# Revit family: СКМ-2К DN15-40 (резьба)
name_source: partatom
category: Арматура трубопроводов
revit_build: Autodesk Revit 2015 (Build: 20140322_1515(x64)
units: mm (PartAtom-declared; Revit-internal decimal feet)

## types (8) — shared parameters
URL = http://vogez.by
Видимость клапана = Да
Длина привода = 4 1/4"
Изготовитель = ООО "ВОГЕЗЭНЕРГО"
Класс точности = 2
Максимальная температура среды = 150 °C
Материал и цвет остальных элементов = Сталь, неокрашенная
Материал и цвет привода ППР = Пластик, серый
Материал и цвет теплосчётчика = Латунь
Наименование = Теплосчётчик
Номинальное давление PN = 1.6 МПа
Скругления привода = 3/4"
Степень защиты = IP55
Ширина привода = 3 1/4"

## per-type parameters (varying)
| type | Высота основания привода | Высота с приводом | Диаметр корпуса | Диаметр условный | Диаметр штока | Максимальный расход | Масса | Минимальный расход | Монтажная длина | Номинальный расход | Обозначение | Тип, марка |
| Теплосчётчик СКМ-2К DN15, q=1,5 м3/ч, L=110 мм | 1 3/4" | 3 1/4" | 3/4" | 1/2" | 3/4" | 3.0 м³/ч | 1.00 kg | 0.0 м³/ч | 4 1/4" | 1.5 м³/ч | СКМ-2К-15-16-55-200 | СКМ-2К-15-16-55-200 |
| Теплосчётчик СКМ-2К DN15, q=1,5 м3/ч, L=165 мм | 1 3/4" | 3 1/4" | 3/4" | 1/2" | 3/4" | 3.0 м³/ч | 1.00 kg | 0.0 м³/ч | 6 1/2" | 1.5 м³/ч | СКМ-2К-15-16-55-200 | СКМ-2К-15-16-55-200 |
| Теплосчётчик СКМ-2К DN20, q=1,5 м3/ч, L=190 мм | 2" | 3 1/2" | 1" | 3/4" | 1" | 5.0 м³/ч | 2.00 kg | 0.1 м³/ч | 7 1/2" | 1.5 м³/ч | СКМ-2К-20-16-55-200 | СКМ-2К-20-16-55-200 |
| Теплосчётчик СКМ-2К DN20, q=2,5 м3/ч, L=190 мм | 2" | 3 1/2" | 1" | 3/4" | 1" | 5.0 м³/ч | 2.00 kg | 0.1 м³/ч | 7 1/2" | 2.5 м³/ч | СКМ-2К-20-16-55-200 | СКМ-2К-20-16-55-200 |
| Теплосчётчик СКМ-2К DN25, q=3,5 м3/ч, L=260 мм | 2 1/4" | 3 3/4" | 1 1/4" | 1" | 1 1/4" | 7.0 м³/ч | 3.00 kg | 0.1 м³/ч | 10 1/4" | 3.5 м³/ч | СКМ-2К-25-16-55-200 | СКМ-2К-25-16-55-200 |
| Теплосчётчик СКМ-2К DN25, q=6,0 м3/ч, L=260 мм | 2 1/4" | 3 3/4" | 1 1/4" | 1" | 1 1/4" | 7.0 м³/ч | 3.00 kg | 0.1 м³/ч | 10 1/4" | 6.0 м³/ч | СКМ-2К-25-16-55-200 | СКМ-2К-25-16-55-200 |
| Теплосчётчик СКМ-2К DN32, q=6,0 м3/ч, L=260 мм | 2 1/2" | 4" | 1 1/2" | 1 1/4" | 1 1/2" | 12.0 м³/ч | 6.00 kg | 0.1 м³/ч | 10 1/4" | 6.0 м³/ч | СКМ-2К-32-16-55-200 | СКМ-2К-32-16-55-200 |
| Теплосчётчик СКМ-2К DN40, q=10 м3/ч, L=300 мм | 3" | 4 1/2" | 2" | 1 1/2" | 2" | 20.0 м³/ч | 8.00 kg | 0.2 м³/ч | 11 3/4" | 10.0 м³/ч | СКМ-2К-40-16-55-200 | СКМ-2К-40-16-55-200 |
